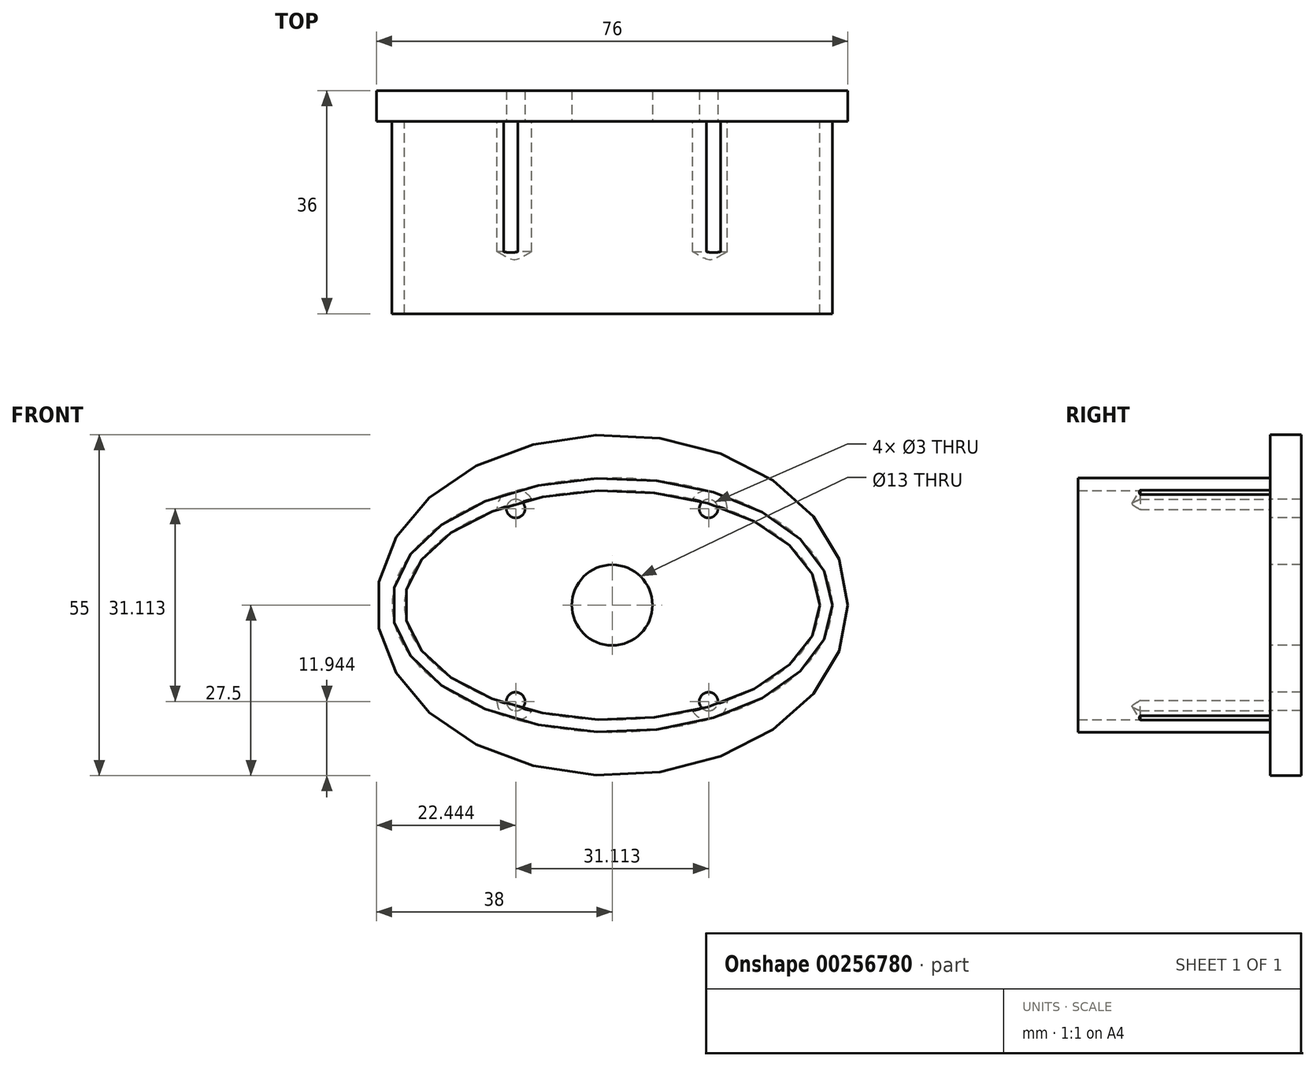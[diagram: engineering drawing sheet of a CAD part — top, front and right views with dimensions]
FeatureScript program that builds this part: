
annotation { "Feature Type Name" : "Feature", "Feature Type Description" : "" }
export const myFeature = defineFeature(function(context is Context, id is Id, definition is map)
    precondition{}
    {
        {
            var Q0;
            Q0=qCreatedBy(makeId("Front.planeOp"),FACE);
            var sketch = newSketch(context, id + "F0", { "sketchPlane" : qUnion([Q0])});
            skEllipse(sketch, "E0", {"center": v(0, 0) * mm, "majorRadius": 35.5 * mm, "minorRadius": 20.5 * mm, "majorAxis": v(1, 0)});
            skEllipse(sketch, "E1", {"center": v(0, 0) * mm, "majorRadius": 33.5 * mm, "minorRadius": 18.5 * mm, "majorAxis": v(1, 0)});
            skSolve(sketch);
        }
        {
            var Q0;
            Q0=makeQuery(id+"F0.imprint","IMPRINT",FACE,{"disambiguationData":[TD([[makeQuery(id+"F0.imprint","IMPRINT",EDGE,{"derivedFrom":sQuery(id+"F0.wireOp",EDGE,"E0")}),1.0]])]});
            var Q1;
            Q1 = qSketchRegion(id + "F2", true);
            extrude(context, id + "F1", {"entities" : qUnion([Q0, Q1]), "depth" : 31 * mm});
        }
        {
            var Q0;
            Q0=qCreatedBy(makeId("Front.planeOp"),FACE);
            var sketch = newSketch(context, id + "F2", { "sketchPlane" : qUnion([Q0])});
            skEllipse(sketch, "E2", {"center": v(0, 0) * mm, "majorRadius": 38 * mm, "minorRadius": 27.5 * mm, "majorAxis": v(1, 0)});
            skSolve(sketch);
        }
        {
            var Q0;
            Q0=makeQuery(id+"F2.imprint","IMPRINT",FACE,{"disambiguationData":[TD([[makeQuery(id+"F2.imprint","IMPRINT",EDGE,{"derivedFrom":sQuery(id+"F2.wireOp",EDGE,"E2")}),1.0]])]});
            var Q1;
            Q1 = qSketchRegion(id + "FChuH8gWBPMXljg_1", true);
            extrude(context, id + "F3", {"entities" : qUnion([Q0, Q1]), "operationType" : NewBodyOperationType.ADD, "oppositeDirection" : true, "depth" : 5 * mm});
        }
        {
            var Q0;
            Q0=sQuery(id+"F2.wireOp",VERTEX,"E2.center");
            var Q1;
            Q1=makeQuery(id+"F1.opExtrude","SWEPT_BODY",BODY,{"disambiguationData":[OSD([sQuery(id+"F0.wireOp",EDGE,"E0"),sQuery(id+"F0.wireOp",EDGE,"E1")])]});
            hole(context, id + "F4", {"style" : HoleStyle.SIMPLE, "endStyle" : HoleEndStyle.BLIND, "holeDiameter" : 13 * mm, "holeDepth" : 5 * mm, "tappedDepth" : 12 * mm, "tapClearance" : 3, "locations" : qUnion([Q0]), "scope" : qUnion([Q1])});
        }
        {
            var Q0;
            Q0=makeQuery(id+"F2.imprint","IMPRINT",FACE,{"disambiguationData":[TD([[makeQuery(id+"F2.imprint","IMPRINT",EDGE,{"derivedFrom":sQuery(id+"F2.wireOp",EDGE,"E2")}),1.0]])]});
            var sketch = newSketch(context, id + "F5", { "sketchPlane" : qUnion([Q0])});
            skPoint(sketch, "E3", {"position": v(15.56, 15.56) * mm});
            skPoint(sketch, "E4.MirrorP", {"position": v(15.56, -15.56) * mm});
            skPoint(sketch, "E5.MirrorP", {"position": v(-15.56, 15.56) * mm});
            skPoint(sketch, "E6.MirrorP", {"position": v(-15.56, -15.56) * mm});
            skSolve(sketch);
        }
        {
            var Q0;
            Q0=sQuery(id+"F5.wireOp",VERTEX,"E5.MirrorP");
            var Q1;
            Q1=sQuery(id+"F5.wireOp",VERTEX,"E3");
            var Q2;
            Q2=sQuery(id+"F5.wireOp",VERTEX,"E6.MirrorP");
            var Q3;
            Q3=sQuery(id+"F5.wireOp",VERTEX,"E4.MirrorP");
            var Q4;
            Q4=makeQuery(id+"F1.opExtrude","SWEPT_BODY",BODY,{"disambiguationData":[OSD([sQuery(id+"F0.wireOp",EDGE,"E0"),sQuery(id+"F0.wireOp",EDGE,"E1")])]});
            hole(context, id + "F6", {"style" : HoleStyle.SIMPLE, "endStyle" : HoleEndStyle.BLIND, "holeDiameter" : 3 * mm, "holeDepth" : 5 * mm, "tappedDepth" : 12 * mm, "tapClearance" : 3, "locations" : qUnion([Q0, Q1, Q2, Q3]), "scope" : qUnion([Q4])});
        }
        {
            var Q0;
            Q0=sQuery(id+"F5.wireOp",VERTEX,"E5.MirrorP");
            var Q1;
            Q1=sQuery(id+"F5.wireOp",VERTEX,"E3");
            var Q2;
            Q2=sQuery(id+"F5.wireOp",VERTEX,"E4.MirrorP");
            var Q3;
            Q3=sQuery(id+"F5.wireOp",VERTEX,"E6.MirrorP");
            var Q4;
            Q4=makeQuery(id+"F1.opExtrude","SWEPT_BODY",BODY,{"disambiguationData":[OSD([sQuery(id+"F0.wireOp",EDGE,"E0"),sQuery(id+"F0.wireOp",EDGE,"E1")])]});
            hole(context, id + "F7", {"style" : HoleStyle.SIMPLE, "endStyle" : HoleEndStyle.BLIND, "oppositeDirection" : true, "holeDiameter" : 6 * mm, "holeDepth" : 21 * mm, "tappedDepth" : 12 * mm, "tapClearance" : 3, "locations" : qUnion([Q0, Q1, Q2, Q3]), "scope" : qUnion([Q4])});
        }
    });
